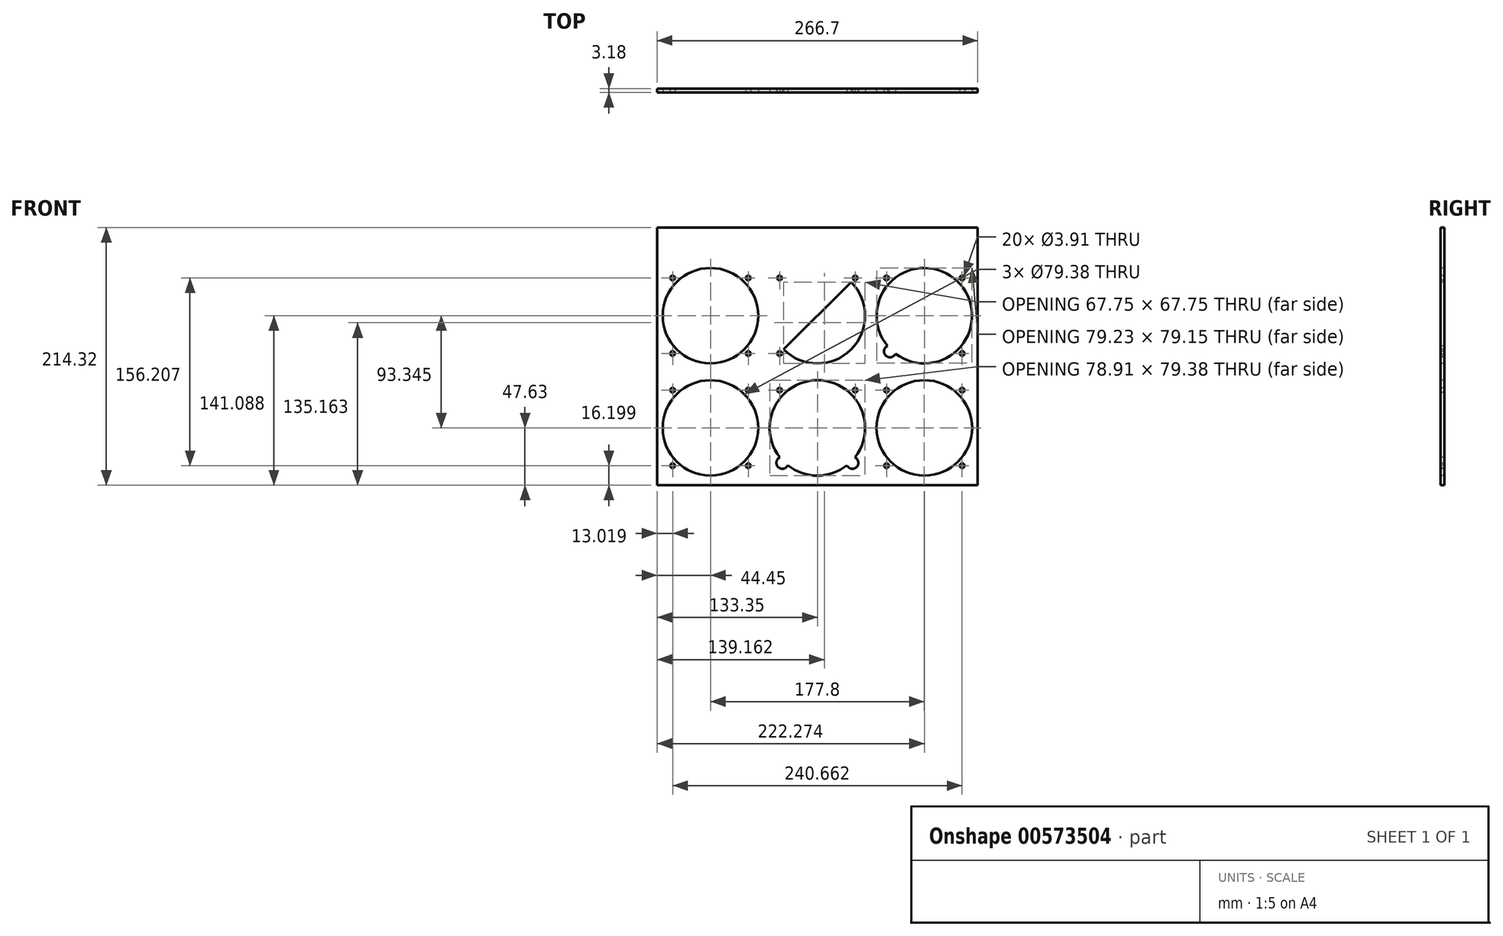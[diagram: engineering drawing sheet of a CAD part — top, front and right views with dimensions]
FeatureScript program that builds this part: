
annotation { "Feature Type Name" : "Feature", "Feature Type Description" : "" }
export const myFeature = defineFeature(function(context is Context, id is Id, definition is map)
    precondition{}
    {
        {
            var Q0;
            Q0=qCreatedBy(makeId("Front.planeOp"),FACE);
            var sketch = newSketch(context, id + "F0", { "sketchPlane" : qUnion([Q0])});
            skLineSegment(sketch, "E0.bottom", {"start": v(146.05, 325.44) * mm, "end": v(412.75, 325.44) * mm});
            skLineSegment(sketch, "E0.top", {"start": v(146.05, 111.13) * mm, "end": v(412.75, 111.13) * mm});
            skLineSegment(sketch, "E0.left", {"start": v(146.05, 325.44) * mm, "end": v(146.05, 111.13) * mm});
            skLineSegment(sketch, "E0.right", {"start": v(412.75, 325.44) * mm, "end": v(412.75, 111.13) * mm});
            skSolve(sketch);
        }
        {
            assignVariable(context, id + "F1", {"name" : "PanelThickness", "anyValue" : 3.17 * mm});
        }
        {
            var Q0;
            Q0=makeQuery(id+"F0.imprint","IMPRINT",FACE,{"disambiguationData":[TD([[makeQuery(id+"F0.imprint","IMPRINT",EDGE,{"derivedFrom":sQuery(id+"F0.wireOp",EDGE,"E0.bottom")}),-1.0]])]});
            extrude(context, id + "F2", {"entities" : qUnion([Q0]), "depth" : getVariable(context, 'PanelThickness'), "offsetDistance" : 25.4 * mm});
        }
        {
            var Q0;
            Q0=makeQuery(id+"F2.opExtrude","CAP_FACE",FACE,{"disambiguationData":[OSD([sQuery(id+"F0.wireOp",EDGE,"E0.bottom"),sQuery(id+"F0.wireOp",EDGE,"E0.top"),sQuery(id+"F0.wireOp",EDGE,"E0.left"),sQuery(id+"F0.wireOp",EDGE,"E0.right")])],"isStart":false});
            var sketch = newSketch(context, id + "F3", { "sketchPlane" : qUnion([Q0])});
            skCircle(sketch, "E1", {"center": v(190.5, 252.1) * mm, "radius": 39.69 * mm});
            skCircle(sketch, "E2", {"center": v(279.4, 252.1) * mm, "radius": 39.69 * mm});
            skCircle(sketch, "E3", {"center": v(368.3, 252.1) * mm, "radius": 39.69 * mm});
            skCircle(sketch, "E4", {"center": v(368.3, 158.75) * mm, "radius": 39.69 * mm});
            skCircle(sketch, "E5", {"center": v(190.5, 158.75) * mm, "radius": 39.69 * mm});
            skCircle(sketch, "E6", {"center": v(279.4, 158.75) * mm, "radius": 39.69 * mm});
            skCircle(sketch, "E7", {"center": v(221.93, 283.53) * mm, "radius": 1.96 * mm});
            skCircle(sketch, "E8", {"center": v(159.07, 283.53) * mm, "radius": 1.96 * mm});
            skCircle(sketch, "E9", {"center": v(221.93, 220.66) * mm, "radius": 1.96 * mm});
            skCircle(sketch, "E10", {"center": v(159.07, 220.66) * mm, "radius": 1.96 * mm});
            skCircle(sketch, "E11.0.1.0", {"center": v(159.07, 190.18) * mm, "radius": 1.96 * mm});
            skCircle(sketch, "E11.0.1.1", {"center": v(221.93, 190.18) * mm, "radius": 1.96 * mm});
            skCircle(sketch, "E11.0.1.2", {"center": v(221.93, 127.32) * mm, "radius": 1.96 * mm});
            skCircle(sketch, "E11.0.1.3", {"center": v(159.07, 127.32) * mm, "radius": 1.96 * mm});
            skCircle(sketch, "E11.1.0.0", {"center": v(247.97, 283.53) * mm, "radius": 1.96 * mm});
            skCircle(sketch, "E11.1.0.1", {"center": v(310.83, 283.53) * mm, "radius": 1.96 * mm});
            skCircle(sketch, "E11.1.0.3", {"center": v(247.97, 220.66) * mm, "radius": 1.96 * mm});
            skCircle(sketch, "E11.1.1.0", {"center": v(247.97, 190.18) * mm, "radius": 1.96 * mm});
            skCircle(sketch, "E11.1.1.1", {"center": v(310.83, 190.18) * mm, "radius": 1.96 * mm});
            skCircle(sketch, "E11.2.0.0", {"center": v(336.87, 283.53) * mm, "radius": 1.96 * mm});
            skCircle(sketch, "E11.2.0.1", {"center": v(399.73, 283.53) * mm, "radius": 1.96 * mm});
            skCircle(sketch, "E11.2.0.2", {"center": v(399.73, 220.66) * mm, "radius": 1.96 * mm});
            skCircle(sketch, "E11.2.1.0", {"center": v(336.87, 190.18) * mm, "radius": 1.96 * mm});
            skCircle(sketch, "E11.2.1.1", {"center": v(399.73, 190.18) * mm, "radius": 1.96 * mm});
            skCircle(sketch, "E11.2.1.2", {"center": v(399.73, 127.32) * mm, "radius": 1.96 * mm});
            skCircle(sketch, "E11.2.1.3", {"center": v(336.87, 127.32) * mm, "radius": 1.96 * mm});
            skLineSegment(sketch, "E11.direction1", {"start": v(159.07, 220.66) * mm, "end": v(247.97, 220.66) * mm, "construction": true});
            skLineSegment(sketch, "E11.direction2", {"start": v(159.07, 220.66) * mm, "end": v(159.07, 127.32) * mm, "construction": true});
            skCircle(sketch, "E12", {"center": v(308.06, 222.56) * mm, "radius": 4.96 * mm});
            skLineSegment(sketch, "E13", {"start": v(247.97, 190.18) * mm, "end": v(308.5, 129.65) * mm});
            skLineSegment(sketch, "E14", {"start": v(310.83, 190.18) * mm, "end": v(250.3, 129.65) * mm});
            skLineSegment(sketch, "E15", {"start": v(399.73, 283.53) * mm, "end": v(339.76, 222.44) * mm});
            skCircle(sketch, "E16", {"center": v(250.3, 129.65) * mm, "radius": 4.96 * mm});
            skCircle(sketch, "E17", {"center": v(339.76, 222.44) * mm, "radius": 4.96 * mm});
            skCircle(sketch, "E18", {"center": v(308.5, 129.65) * mm, "radius": 4.96 * mm});
            skLineSegment(sketch, "E19", {"start": v(336.87, 283.53) * mm, "end": v(399.73, 220.66) * mm});
            skLineSegment(sketch, "E20", {"start": v(310.83, 283.53) * mm, "end": v(247.97, 220.66) * mm});
            skLineSegment(sketch, "E21", {"start": v(159.07, 283.53) * mm, "end": v(221.93, 220.66) * mm});
            skLineSegment(sketch, "E22", {"start": v(221.93, 283.53) * mm, "end": v(159.07, 220.66) * mm});
            skSolve(sketch);
        }
        {
            var Q0;
            {var subQ0=sQuery(id+"F3.wireOp",EDGE,"E13");var subQ1=sQuery(id+"F3.wireOp",EDGE,"E6");var subQ2=makeQuery(id+"F3.imprint","INTERSECT",VERTEX,{"disambiguationData":[OD(0.0)],"derivedFrom":[subQ1,subQ0]});Q0=makeQuery(id+"F3.imprint","IMPRINT",FACE,{"disambiguationData":[TD([[makeQuery(id+"F3.imprint","IMPRINT",EDGE,{"disambiguationData":[TD([[subQ2,-1.0]])],"derivedFrom":subQ1}),1.0]])]});}
            var Q1;
            {var subQ0=sQuery(id+"F3.wireOp",EDGE,"E13");var subQ1=sQuery(id+"F3.wireOp",EDGE,"E6");var subQ2=makeQuery(id+"F3.imprint","INTERSECT",VERTEX,{"disambiguationData":[OD(0.0)],"derivedFrom":[subQ1,subQ0]});Q1=makeQuery(id+"F3.imprint","IMPRINT",FACE,{"disambiguationData":[TD([[makeQuery(id+"F3.imprint","IMPRINT",EDGE,{"disambiguationData":[TD([[subQ2,1.0]])],"derivedFrom":subQ1}),1.0]])]});}
            var Q2;
            Q2=makeQuery(id+"F3.imprint","IMPRINT",FACE,{"disambiguationData":[TD([[makeQuery(id+"F3.imprint","IMPRINT",EDGE,{"derivedFrom":sQuery(id+"F3.wireOp",EDGE,"E1")}),1.0]])]});
            var Q3;
            Q3=makeQuery(id+"F3.imprint","IMPRINT",FACE,{"disambiguationData":[TD([[makeQuery(id+"F3.imprint","IMPRINT",EDGE,{"derivedFrom":sQuery(id+"F3.wireOp",EDGE,"E4")}),1.0]])]});
            var Q4;
            {var subQ0=sQuery(id+"F3.wireOp",EDGE,"E12");var subQ1=sQuery(id+"F3.wireOp",EDGE,"E2");var subQ2=makeQuery(id+"F3.imprint","INTERSECT",VERTEX,{"disambiguationData":[OD(0.0)],"derivedFrom":[subQ1,subQ0]});Q4=makeQuery(id+"F3.imprint","IMPRINT",FACE,{"disambiguationData":[TD([[makeQuery(id+"F3.imprint","IMPRINT",EDGE,{"disambiguationData":[TD([[subQ2,1.0]])],"derivedFrom":subQ1}),1.0]])]});}
            var Q5;
            {var subQ0=sQuery(id+"F3.wireOp",EDGE,"E12");var subQ1=sQuery(id+"F3.wireOp",EDGE,"E2");var subQ2=makeQuery(id+"F3.imprint","INTERSECT",VERTEX,{"disambiguationData":[OD(0.0)],"derivedFrom":[subQ1,subQ0]});Q5=makeQuery(id+"F3.imprint","IMPRINT",FACE,{"disambiguationData":[TD([[makeQuery(id+"F3.imprint","IMPRINT",EDGE,{"disambiguationData":[TD([[subQ2,-1.0]])],"derivedFrom":subQ1}),-1.0]])]});}
            var Q6;
            Q6=makeQuery(id+"F3.imprint","IMPRINT",FACE,{"disambiguationData":[TD([[makeQuery(id+"F3.imprint","IMPRINT",EDGE,{"derivedFrom":sQuery(id+"F3.wireOp",EDGE,"E5")}),1.0]])]});
            var Q7;
            {var subQ0=sQuery(id+"F3.wireOp",EDGE,"E16");var subQ1=sQuery(id+"F3.wireOp",EDGE,"E6");var subQ2=makeQuery(id+"F3.imprint","INTERSECT",VERTEX,{"disambiguationData":[OD(1.0)],"derivedFrom":[subQ1,subQ0]});Q7=makeQuery(id+"F3.imprint","IMPRINT",FACE,{"disambiguationData":[TD([[makeQuery(id+"F3.imprint","IMPRINT",EDGE,{"disambiguationData":[TD([[subQ2,-1.0]])],"derivedFrom":subQ1}),1.0]])]});}
            var Q8;
            {var subQ0=sQuery(id+"F3.wireOp",EDGE,"E14");var subQ1=sQuery(id+"F3.wireOp",EDGE,"E6");var subQ2=makeQuery(id+"F3.imprint","INTERSECT",VERTEX,{"disambiguationData":[OD(0.0)],"derivedFrom":[subQ1,subQ0]});Q8=makeQuery(id+"F3.imprint","IMPRINT",FACE,{"disambiguationData":[TD([[makeQuery(id+"F3.imprint","IMPRINT",EDGE,{"disambiguationData":[TD([[subQ2,1.0]])],"derivedFrom":subQ1}),1.0]])]});}
            var Q9;
            {var subQ0=sQuery(id+"F3.wireOp",EDGE,"E15");var subQ1=sQuery(id+"F3.wireOp",EDGE,"E3");var subQ2=makeQuery(id+"F3.imprint","INTERSECT",VERTEX,{"disambiguationData":[OD(0.0)],"derivedFrom":[subQ1,subQ0]});Q9=makeQuery(id+"F3.imprint","IMPRINT",FACE,{"disambiguationData":[TD([[makeQuery(id+"F3.imprint","IMPRINT",EDGE,{"disambiguationData":[TD([[subQ2,1.0]])],"derivedFrom":subQ1}),1.0]])]});}
            var Q10;
            {var subQ0=sQuery(id+"F3.wireOp",EDGE,"E15");var subQ1=sQuery(id+"F3.wireOp",EDGE,"E3");var subQ2=makeQuery(id+"F3.imprint","INTERSECT",VERTEX,{"disambiguationData":[OD(0.0)],"derivedFrom":[subQ1,subQ0]});Q10=makeQuery(id+"F3.imprint","IMPRINT",FACE,{"disambiguationData":[TD([[makeQuery(id+"F3.imprint","IMPRINT",EDGE,{"disambiguationData":[TD([[subQ2,-1.0]])],"derivedFrom":subQ1}),1.0]])]});}
            var Q11;
            Q11=makeQuery(id+"F3.imprint","IMPRINT",FACE,{"disambiguationData":[TD([[makeQuery(id+"F3.imprint","IMPRINT",EDGE,{"derivedFrom":sQuery(id+"F3.wireOp",EDGE,"E11.2.0.0")}),1.0]])]});
            var Q12;
            Q12=makeQuery(id+"F3.imprint","IMPRINT",FACE,{"disambiguationData":[TD([[makeQuery(id+"F3.imprint","IMPRINT",EDGE,{"derivedFrom":sQuery(id+"F3.wireOp",EDGE,"E8")}),1.0]])]});
            var Q13;
            {var subQ0=sQuery(id+"F3.wireOp",EDGE,"E6");var subQ1=makeQuery(id+"F3.imprint","INTERSECT",VERTEX,{"disambiguationData":[OD(1.0)],"derivedFrom":[subQ0,sQuery(id+"F3.wireOp",EDGE,"E14")]});Q13=makeQuery(id+"F3.imprint","IMPRINT",FACE,{"disambiguationData":[TD([[makeQuery(id+"F3.imprint","IMPRINT",EDGE,{"disambiguationData":[TD([[subQ1,1.0]])],"derivedFrom":subQ0}),-1.0]])]});}
            var Q14;
            {var subQ0=sQuery(id+"F3.wireOp",EDGE,"E14");var subQ1=sQuery(id+"F3.wireOp",EDGE,"E6");var subQ2=makeQuery(id+"F3.imprint","INTERSECT",VERTEX,{"disambiguationData":[OD(1.0)],"derivedFrom":[subQ1,subQ0]});Q14=makeQuery(id+"F3.imprint","IMPRINT",FACE,{"disambiguationData":[TD([[makeQuery(id+"F3.imprint","IMPRINT",EDGE,{"disambiguationData":[TD([[subQ2,1.0]])],"derivedFrom":subQ1}),1.0]])]});}
            var Q15;
            {var subQ0=sQuery(id+"F3.wireOp",EDGE,"E13");var subQ1=sQuery(id+"F3.wireOp",EDGE,"E6");var subQ2=makeQuery(id+"F3.imprint","INTERSECT",VERTEX,{"disambiguationData":[OD(1.0)],"derivedFrom":[subQ1,subQ0]});Q15=makeQuery(id+"F3.imprint","IMPRINT",FACE,{"disambiguationData":[TD([[makeQuery(id+"F3.imprint","IMPRINT",EDGE,{"disambiguationData":[TD([[subQ2,-1.0]])],"derivedFrom":subQ1}),1.0]])]});}
            var Q16;
            {var subQ0=sQuery(id+"F3.wireOp",EDGE,"E14");var subQ1=sQuery(id+"F3.wireOp",EDGE,"E6");var subQ2=makeQuery(id+"F3.imprint","INTERSECT",VERTEX,{"disambiguationData":[OD(1.0)],"derivedFrom":[subQ1,subQ0]});Q16=makeQuery(id+"F3.imprint","IMPRINT",FACE,{"disambiguationData":[TD([[makeQuery(id+"F3.imprint","IMPRINT",EDGE,{"disambiguationData":[TD([[subQ2,-1.0]])],"derivedFrom":subQ1}),1.0]])]});}
            var Q17;
            {var subQ0=sQuery(id+"F3.wireOp",EDGE,"E3");var subQ1=makeQuery(id+"F3.imprint","INTERSECT",VERTEX,{"disambiguationData":[OD(1.0)],"derivedFrom":[subQ0,sQuery(id+"F3.wireOp",EDGE,"E15")]});Q17=makeQuery(id+"F3.imprint","IMPRINT",FACE,{"disambiguationData":[TD([[makeQuery(id+"F3.imprint","IMPRINT",EDGE,{"disambiguationData":[TD([[subQ1,1.0]])],"derivedFrom":subQ0}),-1.0]])]});}
            var Q18;
            {var subQ0=sQuery(id+"F3.wireOp",EDGE,"E15");var subQ1=sQuery(id+"F3.wireOp",EDGE,"E3");var subQ2=makeQuery(id+"F3.imprint","INTERSECT",VERTEX,{"disambiguationData":[OD(1.0)],"derivedFrom":[subQ1,subQ0]});Q18=makeQuery(id+"F3.imprint","IMPRINT",FACE,{"disambiguationData":[TD([[makeQuery(id+"F3.imprint","IMPRINT",EDGE,{"disambiguationData":[TD([[subQ2,-1.0]])],"derivedFrom":subQ1}),1.0]])]});}
            var Q19;
            {var subQ0=sQuery(id+"F3.wireOp",EDGE,"E13");var subQ1=sQuery(id+"F3.wireOp",EDGE,"E6");var subQ2=makeQuery(id+"F3.imprint","INTERSECT",VERTEX,{"disambiguationData":[OD(1.0)],"derivedFrom":[subQ1,subQ0]});Q19=makeQuery(id+"F3.imprint","IMPRINT",FACE,{"disambiguationData":[TD([[makeQuery(id+"F3.imprint","IMPRINT",EDGE,{"disambiguationData":[TD([[subQ2,1.0]])],"derivedFrom":subQ1}),1.0]])]});}
            var Q20;
            {var subQ0=sQuery(id+"F3.wireOp",EDGE,"E15");var subQ1=sQuery(id+"F3.wireOp",EDGE,"E3");var subQ2=makeQuery(id+"F3.imprint","INTERSECT",VERTEX,{"disambiguationData":[OD(1.0)],"derivedFrom":[subQ1,subQ0]});Q20=makeQuery(id+"F3.imprint","IMPRINT",FACE,{"disambiguationData":[TD([[makeQuery(id+"F3.imprint","IMPRINT",EDGE,{"disambiguationData":[TD([[subQ2,1.0]])],"derivedFrom":subQ1}),1.0]])]});}
            var Q21;
            {var subQ0=sQuery(id+"F3.wireOp",EDGE,"E12");var subQ1=sQuery(id+"F3.wireOp",EDGE,"E2");var subQ2=makeQuery(id+"F3.imprint","INTERSECT",VERTEX,{"disambiguationData":[OD(0.0)],"derivedFrom":[subQ1,subQ0]});Q21=makeQuery(id+"F3.imprint","IMPRINT",FACE,{"disambiguationData":[TD([[makeQuery(id+"F3.imprint","IMPRINT",EDGE,{"disambiguationData":[TD([[subQ2,-1.0]])],"derivedFrom":subQ1}),1.0]])]});}
            var Q22;
            Q22=makeQuery(id+"F3.imprint","IMPRINT",FACE,{"disambiguationData":[TD([[makeQuery(id+"F3.imprint","IMPRINT",EDGE,{"derivedFrom":sQuery(id+"F3.wireOp",EDGE,"E11.1.0.1")}),1.0]])]});
            var Q23;
            {var subQ0=sQuery(id+"F3.wireOp",EDGE,"E6");var subQ1=makeQuery(id+"F3.imprint","INTERSECT",VERTEX,{"disambiguationData":[OD(1.0)],"derivedFrom":[subQ0,sQuery(id+"F3.wireOp",EDGE,"E13")]});Q23=makeQuery(id+"F3.imprint","IMPRINT",FACE,{"disambiguationData":[TD([[makeQuery(id+"F3.imprint","IMPRINT",EDGE,{"disambiguationData":[TD([[subQ1,1.0]])],"derivedFrom":subQ0}),-1.0]])]});}
            var Q24;
            Q24=makeQuery(id+"F3.imprint","IMPRINT",FACE,{"disambiguationData":[TD([[makeQuery(id+"F3.imprint","IMPRINT",EDGE,{"derivedFrom":sQuery(id+"F3.wireOp",EDGE,"E7")}),1.0]])]});
            var Q25;
            Q25=makeQuery(id+"F3.imprint","IMPRINT",FACE,{"disambiguationData":[TD([[makeQuery(id+"F3.imprint","IMPRINT",EDGE,{"derivedFrom":sQuery(id+"F3.wireOp",EDGE,"E11.0.1.1")}),1.0]])]});
            var Q26;
            Q26=makeQuery(id+"F3.imprint","IMPRINT",FACE,{"disambiguationData":[TD([[makeQuery(id+"F3.imprint","IMPRINT",EDGE,{"derivedFrom":sQuery(id+"F3.wireOp",EDGE,"E11.2.1.1")}),1.0]])]});
            var Q27;
            Q27=makeQuery(id+"F3.imprint","IMPRINT",FACE,{"disambiguationData":[TD([[makeQuery(id+"F3.imprint","IMPRINT",EDGE,{"derivedFrom":sQuery(id+"F3.wireOp",EDGE,"E11.0.1.3")}),1.0]])]});
            var Q28;
            Q28=makeQuery(id+"F3.imprint","IMPRINT",FACE,{"disambiguationData":[TD([[makeQuery(id+"F3.imprint","IMPRINT",EDGE,{"derivedFrom":sQuery(id+"F3.wireOp",EDGE,"E11.2.1.3")}),1.0]])]});
            var Q29;
            Q29=makeQuery(id+"F3.imprint","IMPRINT",FACE,{"disambiguationData":[TD([[makeQuery(id+"F3.imprint","IMPRINT",EDGE,{"derivedFrom":sQuery(id+"F3.wireOp",EDGE,"E11.2.0.2")}),1.0]])]});
            var Q30;
            Q30=makeQuery(id+"F3.imprint","IMPRINT",FACE,{"disambiguationData":[TD([[makeQuery(id+"F3.imprint","IMPRINT",EDGE,{"derivedFrom":sQuery(id+"F3.wireOp",EDGE,"E11.0.1.2")}),1.0]])]});
            var Q31;
            Q31=makeQuery(id+"F3.imprint","IMPRINT",FACE,{"disambiguationData":[TD([[makeQuery(id+"F3.imprint","IMPRINT",EDGE,{"derivedFrom":sQuery(id+"F3.wireOp",EDGE,"E9")}),1.0]])]});
            var Q32;
            Q32=makeQuery(id+"F3.imprint","IMPRINT",FACE,{"disambiguationData":[TD([[makeQuery(id+"F3.imprint","IMPRINT",EDGE,{"derivedFrom":sQuery(id+"F3.wireOp",EDGE,"E11.2.0.1")}),1.0]])]});
            var Q33;
            Q33=makeQuery(id+"F3.imprint","IMPRINT",FACE,{"disambiguationData":[TD([[makeQuery(id+"F3.imprint","IMPRINT",EDGE,{"derivedFrom":sQuery(id+"F3.wireOp",EDGE,"E11.2.1.2")}),1.0]])]});
            var Q34;
            Q34=makeQuery(id+"F3.imprint","IMPRINT",FACE,{"disambiguationData":[TD([[makeQuery(id+"F3.imprint","IMPRINT",EDGE,{"derivedFrom":sQuery(id+"F3.wireOp",EDGE,"E11.0.1.0")}),1.0]])]});
            var Q35;
            Q35=makeQuery(id+"F3.imprint","IMPRINT",FACE,{"disambiguationData":[TD([[makeQuery(id+"F3.imprint","IMPRINT",EDGE,{"derivedFrom":sQuery(id+"F3.wireOp",EDGE,"E11.2.1.0")}),1.0]])]});
            var Q36;
            Q36=makeQuery(id+"F3.imprint","IMPRINT",FACE,{"disambiguationData":[TD([[makeQuery(id+"F3.imprint","IMPRINT",EDGE,{"derivedFrom":sQuery(id+"F3.wireOp",EDGE,"E11.1.0.0")}),1.0]])]});
            var Q37;
            Q37=makeQuery(id+"F3.imprint","IMPRINT",FACE,{"disambiguationData":[TD([[makeQuery(id+"F3.imprint","IMPRINT",EDGE,{"derivedFrom":sQuery(id+"F3.wireOp",EDGE,"E11.1.0.3")}),1.0]])]});
            var Q38;
            Q38=makeQuery(id+"F3.imprint","IMPRINT",FACE,{"disambiguationData":[TD([[makeQuery(id+"F3.imprint","IMPRINT",EDGE,{"derivedFrom":sQuery(id+"F3.wireOp",EDGE,"E10")}),1.0]])]});
            var Q39;
            Q39=makeQuery(id+"F3.imprint","IMPRINT",FACE,{"disambiguationData":[TD([[makeQuery(id+"F3.imprint","IMPRINT",EDGE,{"derivedFrom":sQuery(id+"F3.wireOp",EDGE,"E11.1.1.0")}),1.0]])]});
            var Q40;
            Q40=makeQuery(id+"F3.imprint","IMPRINT",FACE,{"disambiguationData":[TD([[makeQuery(id+"F3.imprint","IMPRINT",EDGE,{"derivedFrom":sQuery(id+"F3.wireOp",EDGE,"E11.1.1.1")}),1.0]])]});
            var Q41;
            {var subQ0=sQuery(id+"F3.wireOp",EDGE,"E20");var subQ1=sQuery(id+"F3.wireOp",EDGE,"E2");var subQ2=makeQuery(id+"F3.imprint","INTERSECT",VERTEX,{"disambiguationData":[OD(0.0)],"derivedFrom":[subQ1,subQ0]});Q41=makeQuery(id+"F3.imprint","IMPRINT",FACE,{"disambiguationData":[TD([[makeQuery(id+"F3.imprint","IMPRINT",EDGE,{"disambiguationData":[TD([[subQ2,1.0]])],"derivedFrom":subQ1}),1.0]])]});}
            var Q42;
            {var subQ0=sQuery(id+"F3.wireOp",EDGE,"E19");var subQ1=sQuery(id+"F3.wireOp",EDGE,"E3");var subQ2=makeQuery(id+"F3.imprint","INTERSECT",VERTEX,{"disambiguationData":[OD(0.0)],"derivedFrom":[subQ1,subQ0]});Q42=makeQuery(id+"F3.imprint","IMPRINT",FACE,{"disambiguationData":[TD([[makeQuery(id+"F3.imprint","IMPRINT",EDGE,{"disambiguationData":[TD([[subQ2,-1.0]])],"derivedFrom":subQ1}),1.0]])]});}
            var Q43;
            {var subQ0=sQuery(id+"F3.wireOp",EDGE,"E19");var subQ1=sQuery(id+"F3.wireOp",EDGE,"E3");var subQ2=makeQuery(id+"F3.imprint","INTERSECT",VERTEX,{"disambiguationData":[OD(1.0)],"derivedFrom":[subQ1,subQ0]});Q43=makeQuery(id+"F3.imprint","IMPRINT",FACE,{"disambiguationData":[TD([[makeQuery(id+"F3.imprint","IMPRINT",EDGE,{"disambiguationData":[TD([[subQ2,1.0]])],"derivedFrom":subQ1}),1.0]])]});}
            extrude(context, id + "F4", {"entities" : qUnion([Q0, Q1, Q2, Q3, Q4, Q5, Q6, Q7, Q8, Q9, Q10, Q11, Q12, Q13, Q14, Q15, Q16, Q17, Q18, Q19, Q20, Q21, Q22, Q23, Q24, Q25, Q26, Q27, Q28, Q29, Q30, Q31, Q32, Q33, Q34, Q35, Q36, Q37, Q38, Q39, Q40, Q41, Q42, Q43]), "operationType" : NewBodyOperationType.REMOVE, "oppositeDirection" : true, "depth" : 3.17 * mm, "offsetDistance" : 25.4 * mm});
        }
    });
